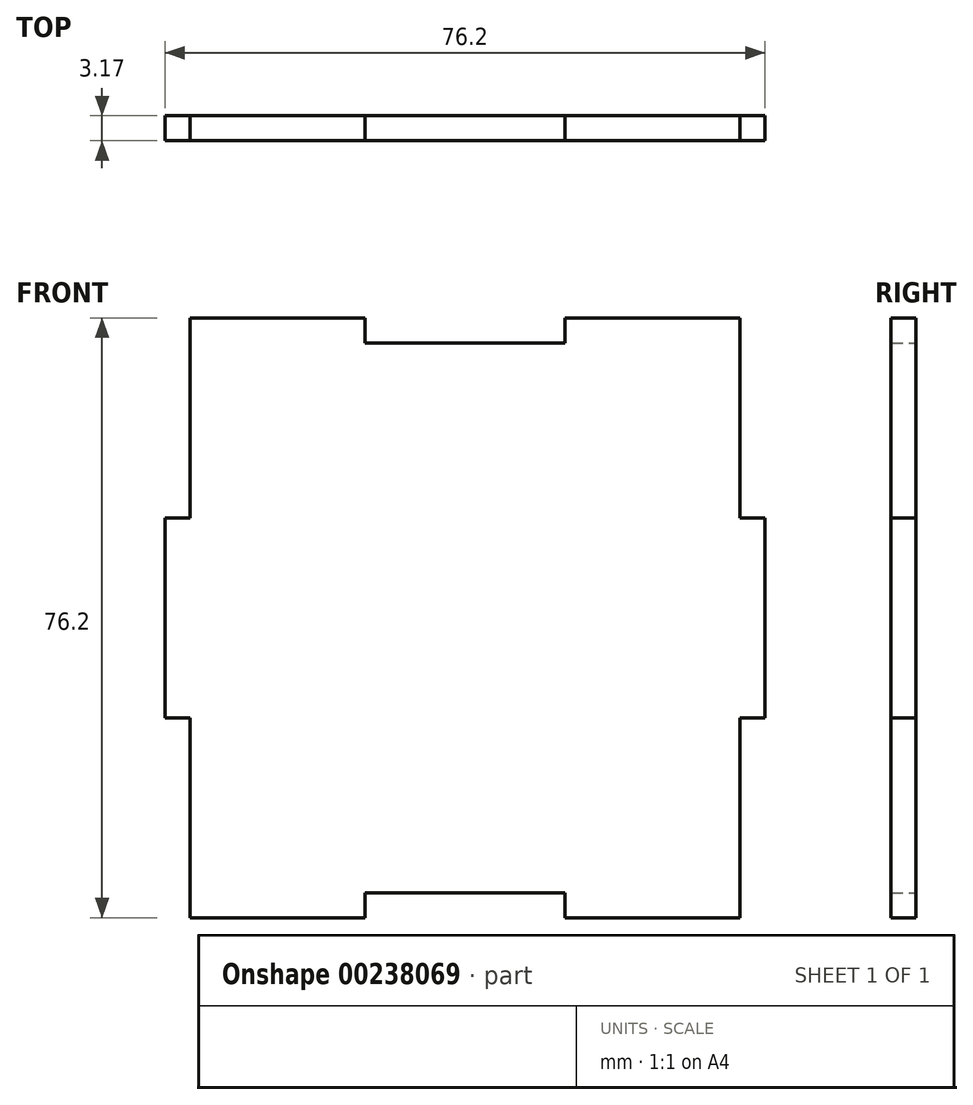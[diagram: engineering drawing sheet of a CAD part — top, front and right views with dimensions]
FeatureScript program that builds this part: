
annotation { "Feature Type Name" : "Feature", "Feature Type Description" : "" }
export const myFeature = defineFeature(function(context is Context, id is Id, definition is map)
    precondition{}
    {
        {
            var Q0;
            Q0=qCreatedBy(makeId("Front.planeOp"),FACE);
            var sketch = newSketch(context, id + "F0", { "sketchPlane" : qUnion([Q0])});
            skLineSegment(sketch, "E0.bottom", {"start": v(34.93, -38.1) * mm, "end": v(-34.93, -38.1) * mm});
            skLineSegment(sketch, "E0.top", {"start": v(34.93, 38.1) * mm, "end": v(-34.93, 38.1) * mm});
            skLineSegment(sketch, "E0.left", {"start": v(34.93, -38.1) * mm, "end": v(34.93, 38.1) * mm});
            skLineSegment(sketch, "E0.right", {"start": v(-34.93, -38.1) * mm, "end": v(-34.93, 38.1) * mm});
            skPoint(sketch, "E0.middle", {"position": v(0, 0) * mm});
            skLineSegment(sketch, "E1.bottom", {"start": v(-12.7, 38.1) * mm, "end": v(12.7, 38.1) * mm});
            skLineSegment(sketch, "E1.top", {"start": v(-12.7, 34.92) * mm, "end": v(12.7, 34.92) * mm});
            skLineSegment(sketch, "E1.left", {"start": v(-12.7, 38.1) * mm, "end": v(-12.7, 34.92) * mm});
            skLineSegment(sketch, "E1.right", {"start": v(12.7, 38.1) * mm, "end": v(12.7, 34.92) * mm});
            skLineSegment(sketch, "E2.MirrorCS", {"start": v(-12.7, -34.92) * mm, "end": v(12.7, -34.92) * mm});
            skLineSegment(sketch, "E3.MirrorCS", {"start": v(-12.7, -38.1) * mm, "end": v(12.7, -38.1) * mm});
            skLineSegment(sketch, "E4.MirrorCS", {"start": v(-12.7, -38.1) * mm, "end": v(-12.7, -34.92) * mm});
            skLineSegment(sketch, "E5.MirrorCS", {"start": v(12.7, -38.1) * mm, "end": v(12.7, -34.92) * mm});
            skLineSegment(sketch, "E6.bottom", {"start": v(-38.1, -12.7) * mm, "end": v(-34.93, -12.7) * mm});
            skLineSegment(sketch, "E6.top", {"start": v(-38.1, 12.7) * mm, "end": v(-34.93, 12.7) * mm});
            skLineSegment(sketch, "E6.left", {"start": v(-34.93, -12.7) * mm, "end": v(-34.93, 12.7) * mm});
            skLineSegment(sketch, "E6.right", {"start": v(-38.1, -12.7) * mm, "end": v(-38.1, 12.7) * mm});
            skLineSegment(sketch, "E7.MirrorCS", {"start": v(38.1, -12.7) * mm, "end": v(38.1, 12.7) * mm});
            skLineSegment(sketch, "E8.MirrorCS", {"start": v(38.1, 12.7) * mm, "end": v(34.93, 12.7) * mm});
            skLineSegment(sketch, "E9.MirrorCS", {"start": v(38.1, -12.7) * mm, "end": v(34.93, -12.7) * mm});
            skSolve(sketch);
        }
        {
            var Q0;
            Q0=makeQuery(id+"F0.imprint","IMPRINT",FACE,{"disambiguationData":[TD([[makeQuery(id+"F0.imprint","IMPRINT",EDGE,{"derivedFrom":sQuery(id+"F0.wireOp",EDGE,"E1.top")}),-1.0]])]});
            var Q1;
            Q1=makeQuery(id+"F0.imprint","IMPRINT",FACE,{"disambiguationData":[TD([[makeQuery(id+"F0.imprint","IMPRINT",EDGE,{"derivedFrom":sQuery(id+"F0.wireOp",EDGE,"E6.bottom")}),1.0]])]});
            var Q2;
            Q2=makeQuery(id+"F0.imprint","IMPRINT",FACE,{"disambiguationData":[TD([[makeQuery(id+"F0.imprint","IMPRINT",EDGE,{"derivedFrom":sQuery(id+"F0.wireOp",EDGE,"E7.MirrorCS")}),1.0]])]});
            extrude(context, id + "F1", {"entities" : qUnion([Q0, Q1, Q2]), "depth" : 3.17 * mm});
        }
    });
